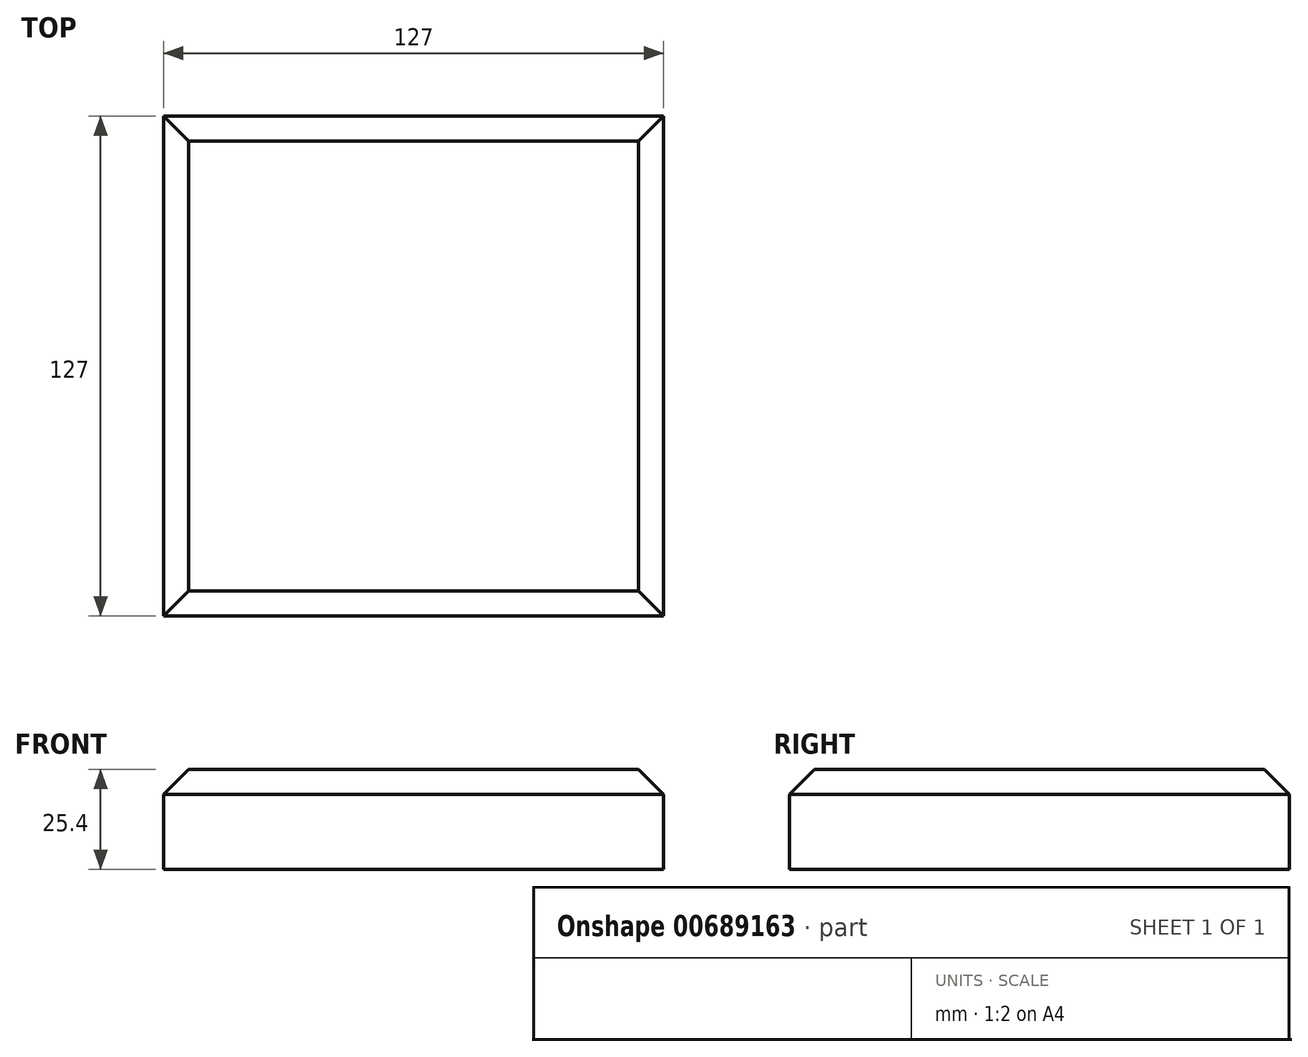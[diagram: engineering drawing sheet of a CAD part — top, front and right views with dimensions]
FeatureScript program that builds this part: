
annotation { "Feature Type Name" : "Feature", "Feature Type Description" : "" }
export const myFeature = defineFeature(function(context is Context, id is Id, definition is map)
    precondition{}
    {
        {
            var Q0;
            Q0=qCreatedBy(makeId("Top.planeOp"),FACE);
            var sketch = newSketch(context, id + "F0", { "sketchPlane" : qUnion([Q0])});
            skLineSegment(sketch, "E0.bottom", {"start": v(63.5, 63.5) * mm, "end": v(-63.5, 63.5) * mm});
            skLineSegment(sketch, "E0.top", {"start": v(63.5, -63.5) * mm, "end": v(-63.5, -63.5) * mm});
            skLineSegment(sketch, "E0.left", {"start": v(63.5, 63.5) * mm, "end": v(63.5, -63.5) * mm});
            skLineSegment(sketch, "E0.right", {"start": v(-63.5, 63.5) * mm, "end": v(-63.5, -63.5) * mm});
            skPoint(sketch, "E0.middle", {"position": v(0, 0) * mm});
            skSolve(sketch);
        }
        {
            var Q0;
            Q0 = qSketchRegion(id + "F0", true);
            extrude(context, id + "F1", {"entities" : qUnion([Q0]), "depth" : 25.4 * mm, "offsetDistance" : 25.4 * mm});
        }
        {
            var Q0;
            Q0=makeQuery(id+"F1.opExtrude","CAP_EDGE",EDGE,{"disambiguationData":[OSD([sQuery(id+"F0.wireOp",EDGE,"E0.top")])],"isStart":false});
            var Q1;
            Q1=makeQuery(id+"F1.opExtrude","CAP_EDGE",EDGE,{"disambiguationData":[OSD([sQuery(id+"F0.wireOp",EDGE,"E0.left")])],"isStart":false});
            var Q2;
            Q2=makeQuery(id+"F1.opExtrude","CAP_EDGE",EDGE,{"disambiguationData":[OSD([sQuery(id+"F0.wireOp",EDGE,"E0.bottom")])],"isStart":false});
            var Q3;
            Q3=makeQuery(id+"F1.opExtrude","CAP_EDGE",EDGE,{"disambiguationData":[OSD([sQuery(id+"F0.wireOp",EDGE,"E0.right")])],"isStart":false});
            chamfer(context, id + "F2", {"entities" : qUnion([Q0, Q1, Q2, Q3]), "width" : 6.35 * mm, "tangentPropagation" : true});
        }
    });
